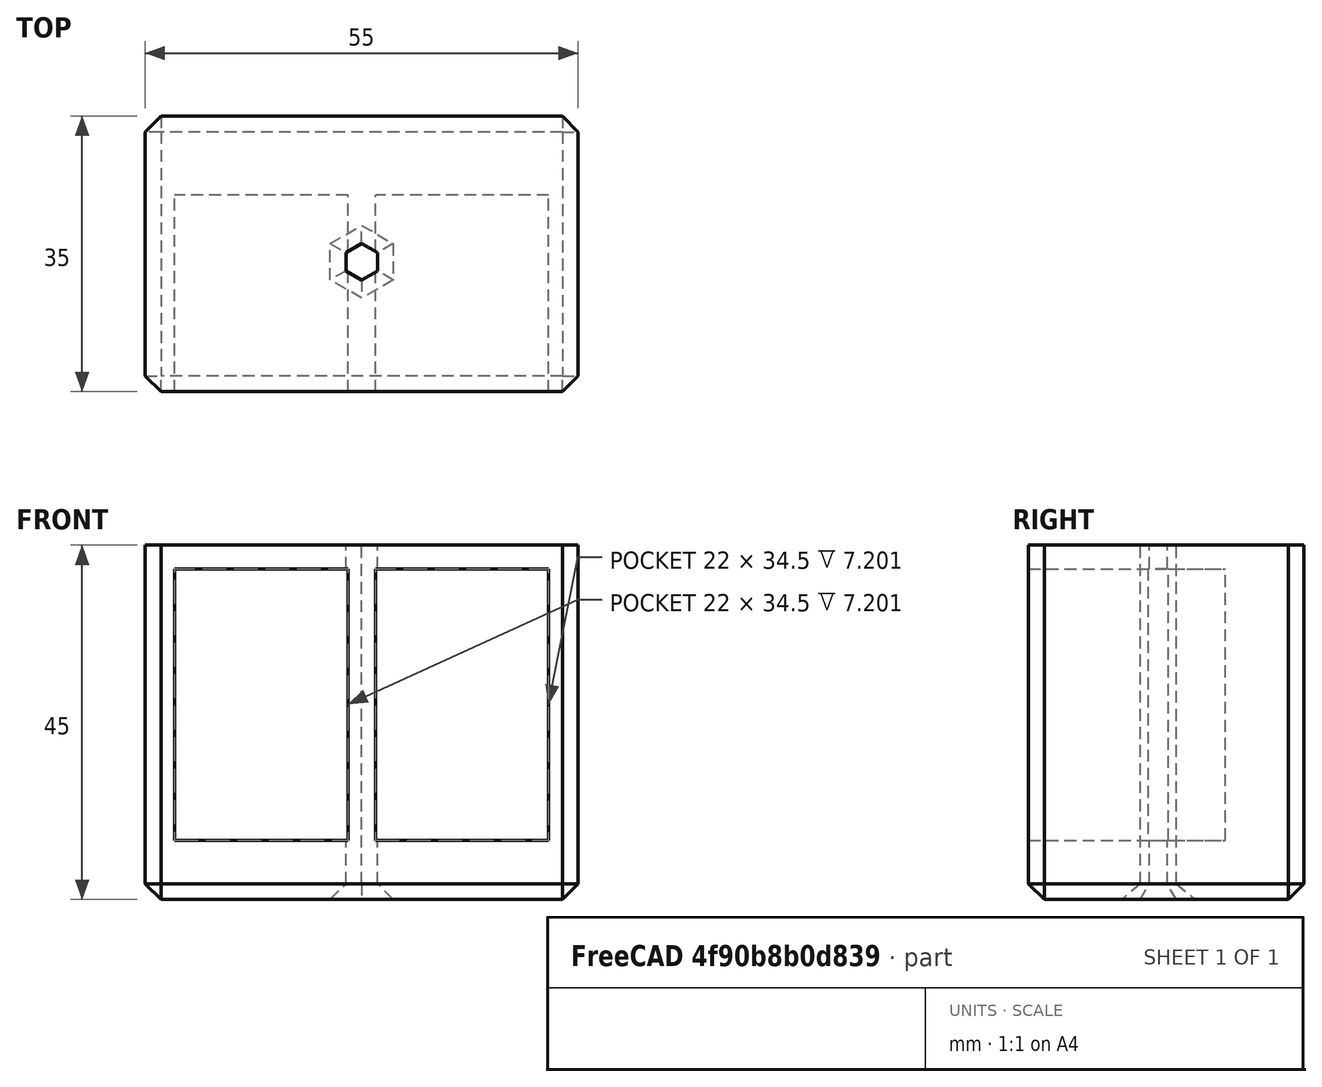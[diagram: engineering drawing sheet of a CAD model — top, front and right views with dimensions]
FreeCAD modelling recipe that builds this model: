
FCSTD DOCUMENT  (FreeCAD 0.19R)
Label: HexHolder
License: All rights reserved
LicenseURL: http://en.wikipedia.org/wiki/All_rights_reserved
objects: Sketcher::SketchObject×4, PartDesign::Pocket×2, PartDesign::Chamfer×2, PartDesign::Pad×1, PartDesign::Body×1, Mesh::Feature×1
note: 15 computed .brp shape members not serialized (recipe doc carries the construction recipe); baked Part::Feature solids carry a one-line shape summary decoded from their .brp

FEATURE [Sketcher::SketchObject] Sketch
  FullyConstrained = true
  MapMode = 5
  Placement = pos=(0,0,0) rot=(1,0,0;1.5708rad)
  Support = -> [XZ_Plane]
  sketch-geometry (4):
    g0: LineSegment StartX=-27.5 StartY=0 StartZ=0 EndX=27.5 EndY=0 EndZ=0
    g1: LineSegment StartX=27.5 StartY=0 StartZ=0 EndX=27.5 EndY=-45 EndZ=0
    g2: LineSegment StartX=27.5 StartY=-45 StartZ=0 EndX=-27.5 EndY=-45 EndZ=0
    g3: LineSegment StartX=-27.5 StartY=-45 StartZ=0 EndX=-27.5 EndY=0 EndZ=0
  constraints (11):
    c: Coincident(g0,g1)
    c: Coincident(g1,g2)
    c: Coincident(g2,g3)
    c: Coincident(g3,g0)
    c: Horizontal(g2)
    c: Vertical(g1)
    c: Vertical(g3)
    c: PointOnObject(g0,g-1)
    c: Symmetric(g0,g0,g-2)
    c: Distance(g1) = 45
    c: Distance(g0) = 55
FEATURE [PartDesign::Pad] Pad
  Direction = (1,1,1)
  Length = 35
  Length2 = 100
  Placement = pos=(0,0,0) rot=(1,0,0;1.5708rad)
  Profile = -> Sketch
  Type = 0
FEATURE [Sketcher::SketchObject] Sketch001
  FullyConstrained = true
  MapMode = 5
  Placement = pos=(0,-35,2.33e-14) rot=(1,0,0;1.5708rad)
  Support = -> [Pad]
  sketch-geometry (8):
    g0: LineSegment StartX=-23.75 StartY=-3 StartZ=0 EndX=-1.75 EndY=-3 EndZ=0
    g1: LineSegment StartX=-1.75 StartY=-3 StartZ=0 EndX=-1.75 EndY=-37.5 EndZ=0
    g2: LineSegment StartX=-1.75 StartY=-37.5 StartZ=0 EndX=-23.75 EndY=-37.5 EndZ=0
    g3: LineSegment StartX=-23.75 StartY=-37.5 StartZ=0 EndX=-23.75 EndY=-3 EndZ=0
    g4: LineSegment StartX=1.75 StartY=-3 StartZ=0 EndX=23.75 EndY=-3 EndZ=0
    g5: LineSegment StartX=23.75 StartY=-3 StartZ=0 EndX=23.75 EndY=-37.5 EndZ=0
    g6: LineSegment StartX=23.75 StartY=-37.5 StartZ=0 EndX=1.75 EndY=-37.5 EndZ=0
    g7: LineSegment StartX=1.75 StartY=-37.5 StartZ=0 EndX=1.75 EndY=-3 EndZ=0
  constraints (23):
    c: Coincident(g0,g1)
    c: Coincident(g1,g2)
    c: Coincident(g2,g3)
    c: Coincident(g3,g0)
    c: Horizontal(g0)
    c: Horizontal(g2)
    c: Vertical(g1)
    c: Vertical(g3)
    c: Coincident(g4,g5)
    c: Coincident(g5,g6)
    c: Coincident(g6,g7)
    c: Coincident(g7,g4)
    c: Horizontal(g4)
    c: Horizontal(g6)
    c: Vertical(g5)
    c: Vertical(g7)
    c: Equal(g0,g4)
    c: Distance(g0) = 22
    c: Distance(g3) = 34.5
    c: Equal(g3,g7)
    c: Symmetric(g4,g0,g-2)
    c: Distance(g4,g1) = 3.5
    c: DistanceY(g4) = -3
FEATURE [PartDesign::Pocket] Pocket
  BaseFeature = -> Pad
  Length = 25
  Length2 = 100
  Placement = pos=(0,0,0) rot=(1,0,0;1.5708rad)
  Profile = -> Sketch001
  Type = 0
FEATURE [PartDesign::Chamfer] Chamfer
  Angle = 45
  Base = -> Pocket [Edge8,Edge5,Edge11,Edge9,Edge6,Edge7,Edge12,Edge10]
  BaseFeature = -> Pocket
  ChamferType = 0
  FlipDirection = false
  Placement = pos=(0,0,0) rot=(1,0,0;1.5708rad)
  Size = 2
  Size2 = 1
  SupportTransform = false
FEATURE [Sketcher::SketchObject] Sketch002
  FullyConstrained = true
  MapMode = 5
  Placement = pos=(0,-5e-14,-45) rot=(1,0,0;3.14159rad)
  Support = -> [Chamfer]
  sketch-geometry (7):
    g0: LineSegment StartX=-9.415e-13 StartY=16.1906 StartZ=0 EndX=2 EndY=17.3453 EndZ=0
    g1: LineSegment StartX=2 StartY=17.3453 StartZ=0 EndX=2 EndY=19.6547 EndZ=0
    g2: LineSegment StartX=2 StartY=19.6547 StartZ=0 EndX=-9.415e-13 EndY=20.8094 EndZ=0
    g3: LineSegment StartX=-9.415e-13 StartY=20.8094 StartZ=0 EndX=-2 EndY=19.6547 EndZ=0
    g4: LineSegment StartX=-2 StartY=19.6547 StartZ=0 EndX=-2 EndY=17.3453 EndZ=0
    g5: LineSegment StartX=-2 StartY=17.3453 StartZ=0 EndX=-9.415e-13 EndY=16.1906 EndZ=0
    g6: Circle CenterX=0 CenterY=18.5 CenterZ=0 NormalX=0 NormalY=0 NormalZ=1 AngleXU=0 Radius=2.3094
  constraints (17):
    c: Coincident(g0,g1)
    c: Coincident(g1,g2)
    c: Coincident(g2,g3)
    c: Coincident(g3,g4)
    c: Coincident(g4,g5)
    c: Coincident(g5,g0)
    c: Equal(g0, g1-g5) x5
    c: PointOnObject(g0,g6)
    c: PointOnObject(g1,g6)
    c: PointOnObject(g2,g6)
    c: PointOnObject(g3,g6)
    c: PointOnObject(g4,g6)
    c: PointOnObject(g5,g6)
    c: Distance(g1,g3) = 4
    c: Vertical(g1)
    c: DistanceX(g6) = 0
    c: DistanceY(g6) = 18.5
FEATURE [PartDesign::Pocket] Pocket001
  BaseFeature = -> Chamfer
  Length = 5
  Length2 = 100
  Placement = pos=(0,0,0) rot=(1,0,0;1.5708rad)
  Profile = -> Sketch002
  Type = 1
FEATURE [Sketcher::SketchObject] Sketch003
  FullyConstrained = true
  MapMode = 5
  Placement = pos=(0,-6.99e-14,-45) rot=(1,0,0;3.14159rad)
  Support = -> [Pocket001]
  sketch-geometry (7):
    g0: LineSegment StartX=4 StartY=16.1906 StartZ=0 EndX=4 EndY=20.8094 EndZ=0
    g1: LineSegment StartX=4 StartY=20.8094 StartZ=0 EndX=0 EndY=23.1188 EndZ=0
    g2: LineSegment StartX=3e-16 StartY=23.1188 StartZ=0 EndX=-4 EndY=20.8094 EndZ=0
    g3: LineSegment StartX=-4 StartY=20.8094 StartZ=0 EndX=-4 EndY=16.1906 EndZ=0
    g4: LineSegment StartX=-4 StartY=16.1906 StartZ=0 EndX=-9e-16 EndY=13.8812 EndZ=0
    g5: LineSegment StartX=-9e-16 StartY=13.8812 StartZ=0 EndX=4 EndY=16.1906 EndZ=0
    g6: Circle CenterX=0 CenterY=18.5 CenterZ=0 NormalX=0 NormalY=0 NormalZ=1 AngleXU=0 Radius=4.6188
  constraints (17):
    c: Coincident(g0,g1)
    c: Coincident(g1,g2)
    c: Coincident(g2,g3)
    c: Coincident(g3,g4)
    c: Coincident(g4,g5)
    c: Coincident(g5,g0)
    c: Equal(g0, g1-g5) x5
    c: PointOnObject(g0,g6)
    c: PointOnObject(g1,g6)
    c: PointOnObject(g2,g6)
    c: PointOnObject(g3,g6)
    c: PointOnObject(g4,g6)
    c: PointOnObject(g5,g6)
    c: Vertical(g0)
    c: Distance(g0,g3) = 8
    c: PointOnObject(g6,g-2)
    c: DistanceY(g6) = 18.5
FEATURE [PartDesign::Chamfer] Chamfer001
  Angle = 45
  Base = -> Pocket001 [Edge99,Edge60,Edge54,Edge100,Edge46,Edge39]
  BaseFeature = -> Pocket001
  ChamferType = 0
  FlipDirection = false
  Placement = pos=(0,0,0) rot=(1,0,0;1.5708rad)
  Size = 2
  Size2 = 1
  SupportTransform = false
FEATURE [PartDesign::Body] Body
  Group = -> [Sketch,Pad,Sketch001,Pocket,Chamfer,Sketch002,Sketch003,Pocket001,Chamfer001]
  Origin = -> Origin
  Tip = -> Chamfer001
FEATURE [Mesh::Feature] Mesh  label="Chamfer001 (Meshed)"
